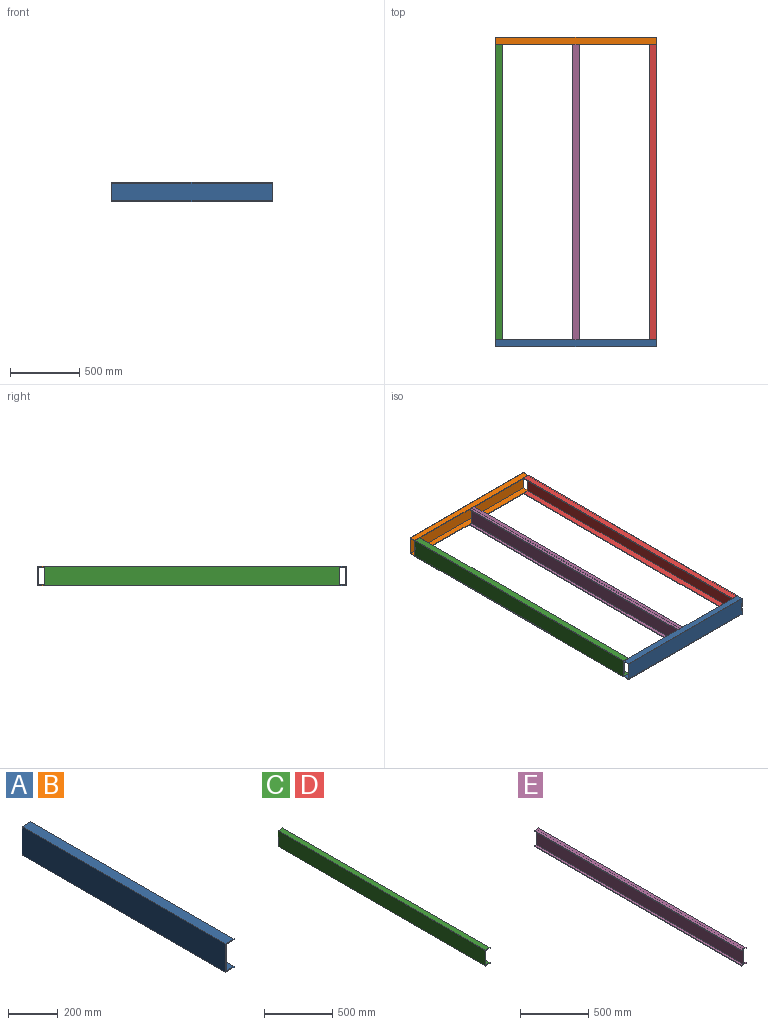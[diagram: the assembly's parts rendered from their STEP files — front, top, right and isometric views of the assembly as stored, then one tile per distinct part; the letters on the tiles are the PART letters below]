
ASSEMBLY  parts=5 mates=3
PART A: 10 faces, bbox 50x1160x140 mm
  f0: plane 1160x5mm, normal (1,0,0), area 5800mm2, adj f1,f3,f6,f9
  f1: plane 140x50mm, normal (0,1,0), area 1150mm2, adj f0,f2,f4,f5,f6,f7,f8,f9
  f2: plane 1160x5mm, normal (1,0,0), area 5800mm2, adj f1,f3,f5,f8
  f3: plane 140x50mm, normal (0,-1,0), area 1150mm2, adj f0,f2,f4,f5,f6,f7,f8,f9
  f4: plane 1160x130mm, normal (1,0,0), area 150800mm2, adj f1,f3,f5,f6
  f5: plane 1160x45mm, normal (0,0,-1), area 52200mm2, adj f1,f2,f3,f4
  f6: plane 1160x45mm, normal (0,0,1), area 52200mm2, adj f0,f1,f3,f4
  f7: plane 1160x140mm, normal (-1,0,0), area 162400mm2, adj f1,f3,f8,f9
  f8: plane 1160x50mm, normal (0,0,1), area 58000mm2, adj f1,f2,f3,f7
  f9: plane 1160x50mm, normal (0,0,-1), area 58000mm2, adj f0,f1,f3,f7
PART B: same geometry as A
PART C: 10 faces, bbox 50x2140x140 mm
  f0: plane 2140x5mm, normal (1,0,0), area 10700mm2, adj f1,f3,f6,f9
  f1: plane 140x50mm, normal (0,1,0), area 1150mm2, adj f0,f2,f4,f5,f6,f7,f8,f9
  f2: plane 2140x5mm, normal (1,0,0), area 10700mm2, adj f1,f3,f5,f8
  f3: plane 140x50mm, normal (0,-1,0), area 1150mm2, adj f0,f2,f4,f5,f6,f7,f8,f9
  f4: plane 2140x130mm, normal (1,0,0), area 278200mm2, adj f1,f3,f5,f6
  f5: plane 2140x45mm, normal (0,0,-1), area 96300mm2, adj f1,f2,f3,f4
  f6: plane 2140x45mm, normal (0,0,1), area 96300mm2, adj f0,f1,f3,f4
  f7: plane 2140x140mm, normal (-1,0,0), area 299600mm2, adj f1,f3,f8,f9
  f8: plane 2140x50mm, normal (0,0,1), area 107000mm2, adj f1,f2,f3,f7
  f9: plane 2140x50mm, normal (0,0,-1), area 107000mm2, adj f0,f1,f3,f7
PART D: same geometry as C
PART E: 14 faces, bbox 50x2140x140 mm
  f0: plane 2140x50mm, normal (0,0,1), area 107000mm2, adj f1,f11,f12,f13
  f1: plane 2140x5mm, normal (-1,0,0), area 10700mm2, adj f0,f2,f12,f13
  f2: plane 2140x22.5mm, normal (0,0,-1), area 48150mm2, adj f1,f3,f12,f13
  f3: plane 2140x130mm, normal (-1,0,0), area 278200mm2, adj f2,f4,f12,f13
  f4: plane 2140x22.5mm, normal (0,0,1), area 48150mm2, adj f3,f5,f12,f13
  f5: plane 2140x5mm, normal (-1,0,0), area 10700mm2, adj f4,f6,f12,f13
  f6: plane 2140x50mm, normal (0,0,-1), area 107000mm2, adj f5,f7,f12,f13
  f7: plane 2140x5mm, normal (1,0,0), area 10700mm2, adj f6,f8,f12,f13
  f8: plane 2140x22.5mm, normal (0,0,1), area 48150mm2, adj f7,f9,f12,f13
  f9: plane 2140x130mm, normal (1,0,0), area 278200mm2, adj f8,f10,f12,f13
  f10: plane 2140x22.5mm, normal (0,0,-1), area 48150mm2, adj f9,f11,f12,f13
  f11: plane 2140x5mm, normal (1,0,0), area 10700mm2, adj f0,f10,f12,f13
  f12: plane 140x50mm, normal (0,-1,0), area 1150mm2, adj f0,f1,f2,f3,f4,f5,f6,f7
  f13: plane 140x50mm, normal (0,1,0), area 1150mm2, adj f0,f1,f2,f3,f4,f5,f6,f7
PLACE A rot(axis=(0,0,1),90deg) t=(-580,-2190,0)mm
PLACE B rot(axis=(0,0,-1),90deg) t=(580,50,0)mm
PLACE C t=(-580,0,0)mm
PLACE D rot(axis=(0,0,1),180deg) t=(580,-2140,0)mm
PLACE E at identity
MATE fastened D.f8 <-> A.f8  axis (0,0,1) through (580,-2140,140)mm
MATE fastened A.f8 <-> E.f0  axis (0,0,1) through (0,-2140,140)mm
MATE fastened C.f8 <-> A.f8  axis (0,0,1) through (-580,-2140,140)mm
